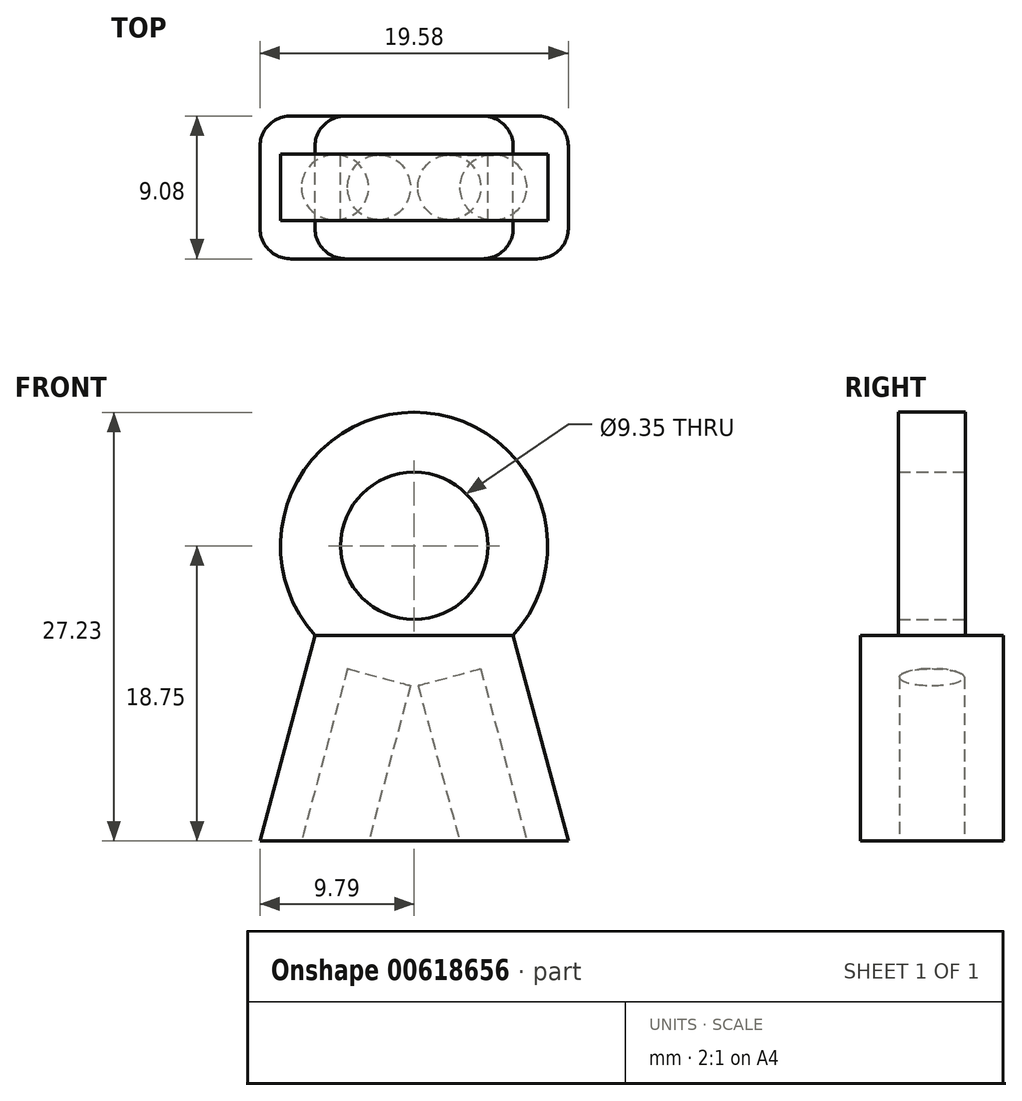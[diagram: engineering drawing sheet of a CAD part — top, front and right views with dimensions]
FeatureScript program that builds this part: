
annotation { "Feature Type Name" : "Feature", "Feature Type Description" : "" }
export const myFeature = defineFeature(function(context is Context, id is Id, definition is map)
    precondition{}
    {
        {
            var Q0;
            Q0=qCreatedBy(makeId("Front.planeOp"),FACE);
            var sketch = newSketch(context, id + "F0", { "sketchPlane" : qUnion([Q0])});
            skCircle(sketch, "E0", {"center": v(0, 0) * mm, "radius": 4.68 * mm});
            skCircle(sketch, "E1", {"center": v(0, 0) * mm, "radius": 8.48 * mm});
            skSolve(sketch);
        }
        {
            var Q0;
            Q0 = qSketchRegion(id + "F0", true);
            extrude(context, id + "F1", {"entities" : qUnion([Q0]), "endBound" : BoundingType.SYMMETRIC, "depth" : 4.25 * mm, "offsetDistance" : 25.4 * mm});
        }
        {
            var Q0;
            Q0=qCreatedBy(makeId("Front.planeOp"),FACE);
            var sketch = newSketch(context, id + "F2", { "sketchPlane" : qUnion([Q0])});
            skLineSegment(sketch, "E2", {"start": v(0, 0) * mm, "end": v(-6.5, -24.27) * mm, "construction": true});
            skLineSegment(sketch, "E3", {"start": v(0, 0) * mm, "end": v(7.36, -27.45) * mm, "construction": true});
            skLineSegment(sketch, "E4", {"start": v(0, 0) * mm, "end": v(0, -24.9) * mm, "construction": true});
            skLineSegment(sketch, "E5", {"start": v(-4.23, -7.8) * mm, "end": v(0, -8.93) * mm, "construction": true});
            skLineSegment(sketch, "E6", {"start": v(0, -8.93) * mm, "end": v(4.23, -7.8) * mm, "construction": true});
            skLineSegment(sketch, "E7", {"start": v(-4.23, -7.8) * mm, "end": v(-6.86, -17.62) * mm, "construction": true});
            skLineSegment(sketch, "E8", {"start": v(0, -8.93) * mm, "end": v(-2.63, -18.75) * mm, "construction": true});
            skLineSegment(sketch, "E9", {"start": v(-9.79, -18.75) * mm, "end": v(9.79, -18.75) * mm});
            skLineSegment(sketch, "E10", {"start": v(-9.79, -18.75) * mm, "end": v(-6.3, -5.7) * mm});
            skLineSegment(sketch, "E11", {"start": v(-6.3, -5.7) * mm, "end": v(6.3, -5.7) * mm});
            skLineSegment(sketch, "E12", {"start": v(6.3, -5.7) * mm, "end": v(9.79, -18.75) * mm});
            skSolve(sketch);
        }
        {
            var Q0;
            Q0 = qSketchRegion(id + "F2", true);
            extrude(context, id + "F3", {"entities" : qUnion([Q0]), "operationType" : NewBodyOperationType.ADD, "endBound" : BoundingType.SYMMETRIC, "depth" : 9.08 * mm, "offsetDistance" : 25.4 * mm});
        }
        {
            var Q0;
            Q0=qCreatedBy(makeId("Front.planeOp"),FACE);
            var sketch = newSketch(context, id + "F4", { "sketchPlane" : qUnion([Q0])});
            skLineSegment(sketch, "E13.0", {"start": v(-4.23, -7.8) * mm, "end": v(0, -8.93) * mm});
            skLineSegment(sketch, "E14.0", {"start": v(-4.23, -7.8) * mm, "end": v(-6.86, -17.62) * mm});
            skLineSegment(sketch, "E15.0", {"start": v(0, -8.93) * mm, "end": v(4.23, -7.8) * mm});
            skLineSegment(sketch, "E16", {"start": v(-6.86, -17.62) * mm, "end": v(-7.16, -18.75) * mm});
            skLineSegment(sketch, "E17", {"start": v(-0.24, -8.87) * mm, "end": v(-2.89, -18.75) * mm});
            skLineSegment(sketch, "E18", {"start": v(-2.89, -18.75) * mm, "end": v(-7.16, -18.75) * mm});
            skLineSegment(sketch, "E19", {"start": v(4.23, -7.8) * mm, "end": v(7.16, -18.75) * mm});
            skLineSegment(sketch, "E20", {"start": v(0.24, -8.87) * mm, "end": v(2.89, -18.75) * mm});
            skLineSegment(sketch, "E21", {"start": v(2.89, -18.75) * mm, "end": v(7.16, -18.75) * mm});
            skSolve(sketch);
        }
        {
            var Q0;
            Q0 = qSketchRegion(id + "F4", true);
            extrude(context, id + "F5", {"entities" : qUnion([Q0]), "operationType" : NewBodyOperationType.REMOVE, "endBound" : BoundingType.SYMMETRIC, "oppositeDirection" : true, "depth" : 4.12 * mm, "offsetDistance" : 25.4 * mm});
        }
        {
            var Q0;
            Q0=makeQuery(id+"F5.boolean.opBoolean","COPY",EDGE,{"derivedFrom":makeQuery(id+"F5.opExtrude","CAP_EDGE",EDGE,{"disambiguationData":[OSD([sQuery(id+"F4.wireOp",EDGE,"E14.0"),sQuery(id+"F4.wireOp",EDGE,"E16")])],"isStart":true})});
            var Q1;
            Q1=makeQuery(id+"F5.boolean.opBoolean","COPY",EDGE,{"derivedFrom":makeQuery(id+"F5.opExtrude","CAP_EDGE",EDGE,{"disambiguationData":[OSD([sQuery(id+"F4.wireOp",EDGE,"E20")])],"isStart":true})});
            var Q2;
            Q2=makeQuery(id+"F5.boolean.opBoolean","COPY",EDGE,{"derivedFrom":makeQuery(id+"F5.opExtrude","CAP_EDGE",EDGE,{"disambiguationData":[OSD([sQuery(id+"F4.wireOp",EDGE,"E19")])],"isStart":true})});
            var Q3;
            Q3=makeQuery(id+"F5.boolean.opBoolean","COPY",EDGE,{"derivedFrom":makeQuery(id+"F5.opExtrude","CAP_EDGE",EDGE,{"disambiguationData":[OSD([sQuery(id+"F4.wireOp",EDGE,"E17")])],"isStart":true})});
            var Q4;
            Q4=makeQuery(id+"F5.boolean.opBoolean","COPY",EDGE,{"derivedFrom":makeQuery(id+"F5.opExtrude","CAP_EDGE",EDGE,{"disambiguationData":[OSD([sQuery(id+"F4.wireOp",EDGE,"E19")])],"isStart":false})});
            var Q5;
            Q5=makeQuery(id+"F5.boolean.opBoolean","COPY",EDGE,{"derivedFrom":makeQuery(id+"F5.opExtrude","CAP_EDGE",EDGE,{"disambiguationData":[OSD([sQuery(id+"F4.wireOp",EDGE,"E17")])],"isStart":false})});
            var Q6;
            Q6=makeQuery(id+"F5.boolean.opBoolean","COPY",EDGE,{"derivedFrom":makeQuery(id+"F5.opExtrude","CAP_EDGE",EDGE,{"disambiguationData":[OSD([sQuery(id+"F4.wireOp",EDGE,"E14.0"),sQuery(id+"F4.wireOp",EDGE,"E16")])],"isStart":false})});
            var Q7;
            Q7=makeQuery(id+"F5.boolean.opBoolean","COPY",EDGE,{"derivedFrom":makeQuery(id+"F5.opExtrude","CAP_EDGE",EDGE,{"disambiguationData":[OSD([sQuery(id+"F4.wireOp",EDGE,"E20")])],"isStart":false})});
            fillet(context, id + "F6", {"entities" : qUnion([Q0, Q1, Q2, Q3, Q4, Q5, Q6, Q7]), "radius" : 4.12 * mm / 2, "tangentPropagation" : true, "allowEdgeOverflow" : false});
        }
        {
            var Q0;
            Q0=makeQuery(id+"F3.opExtrude","CAP_EDGE",EDGE,{"disambiguationData":[OSD([sQuery(id+"F2.wireOp",EDGE,"E12")])],"isStart":true});
            var Q1;
            Q1=makeQuery(id+"F3.opExtrude","CAP_EDGE",EDGE,{"disambiguationData":[OSD([sQuery(id+"F2.wireOp",EDGE,"E12")])],"isStart":false});
            var Q2;
            Q2=makeQuery(id+"F3.opExtrude","CAP_EDGE",EDGE,{"disambiguationData":[OSD([sQuery(id+"F2.wireOp",EDGE,"E10")])],"isStart":true});
            var Q3;
            Q3=makeQuery(id+"F3.opExtrude","CAP_EDGE",EDGE,{"disambiguationData":[OSD([sQuery(id+"F2.wireOp",EDGE,"E10")])],"isStart":false});
            fillet(context, id + "F7", {"entities" : qUnion([Q0, Q1, Q2, Q3]), "radius" : 1.9 * mm, "tangentPropagation" : true, "allowEdgeOverflow" : false});
        }
    });
